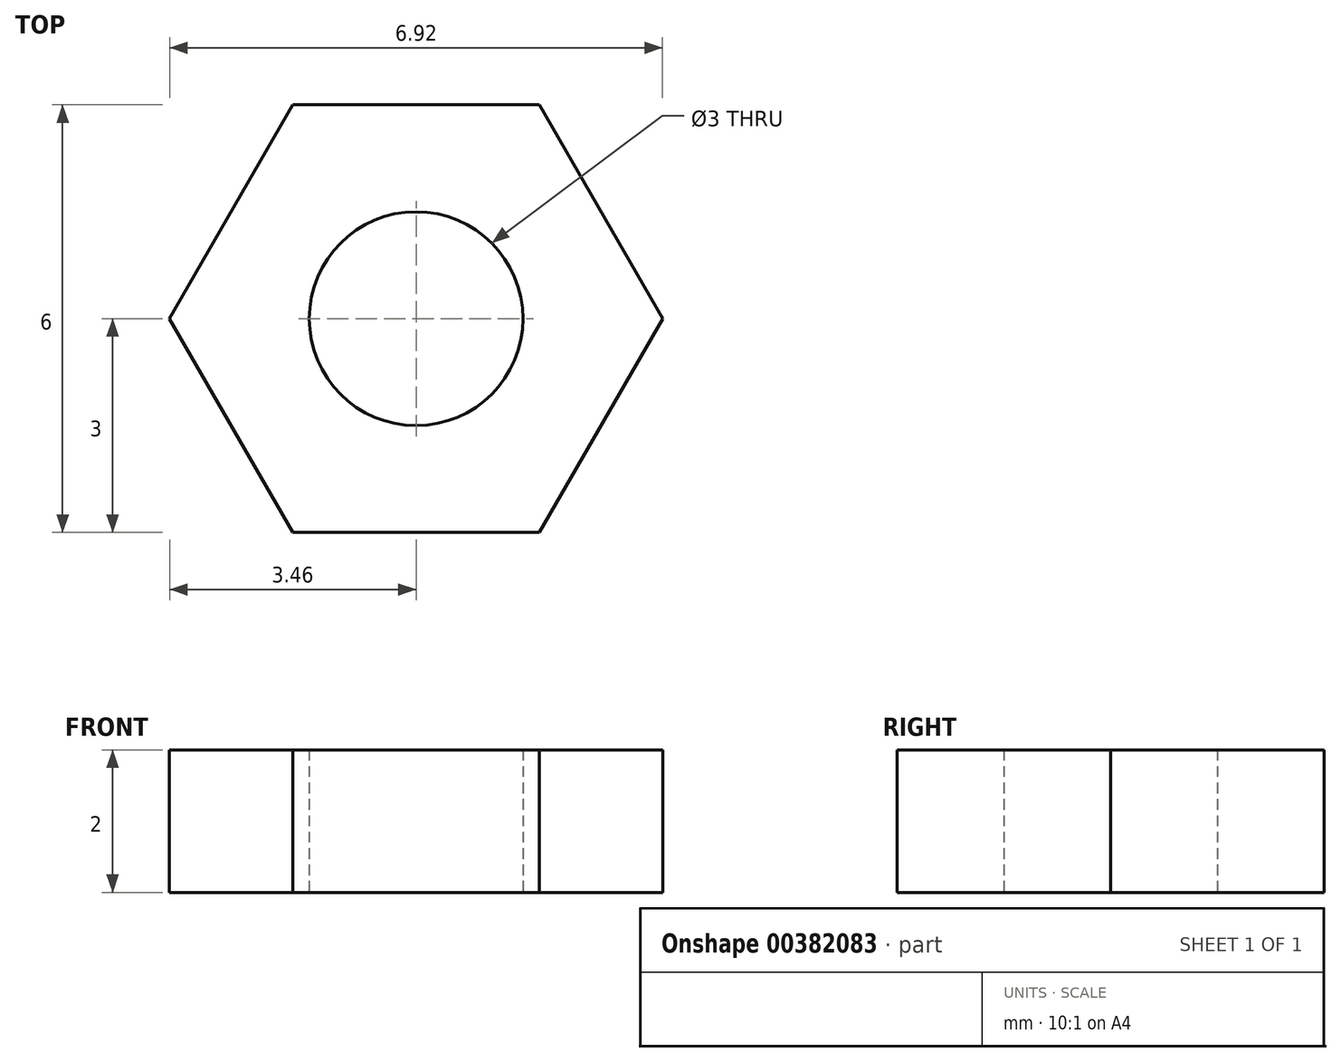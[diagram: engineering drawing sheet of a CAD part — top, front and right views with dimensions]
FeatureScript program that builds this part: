
annotation { "Feature Type Name" : "Feature", "Feature Type Description" : "" }
export const myFeature = defineFeature(function(context is Context, id is Id, definition is map)
    precondition{}
    {
        {
            var Q0;
            Q0=qCreatedBy(makeId("Top.planeOp"),FACE);
            var sketch = newSketch(context, id + "F0", { "sketchPlane" : qUnion([Q0])});
            skCircle(sketch, "E0.cCircle", {"center": v(0, 0) * mm, "radius": 3 * mm, "construction": true});
            skLineSegment(sketch, "E0.0", {"start": v(1.73, -3) * mm, "end": v(-1.73, -3) * mm});
            skLineSegment(sketch, "E0.1", {"start": v(-1.73, -3) * mm, "end": v(-3.46, 0) * mm});
            skLineSegment(sketch, "E0.2", {"start": v(-3.46, 0) * mm, "end": v(-1.73, 3) * mm});
            skLineSegment(sketch, "E0.3", {"start": v(-1.73, 3) * mm, "end": v(1.73, 3) * mm});
            skLineSegment(sketch, "E0.4", {"start": v(1.73, 3) * mm, "end": v(3.46, 0) * mm});
            skLineSegment(sketch, "E0.5", {"start": v(3.46, 0) * mm, "end": v(1.73, -3) * mm});
            skPoint(sketch, "E0.0.midPoint", {"position": v(0, -3) * mm});
            skCircle(sketch, "E1", {"center": v(0, 0) * mm, "radius": 1.5 * mm});
            skSolve(sketch);
        }
        {
            var Q0;
            Q0 = qSketchRegion(id + "F0", true);
            extrude(context, id + "F1", {"entities" : qUnion([Q0]), "depth" : 2 * mm});
        }
    });
